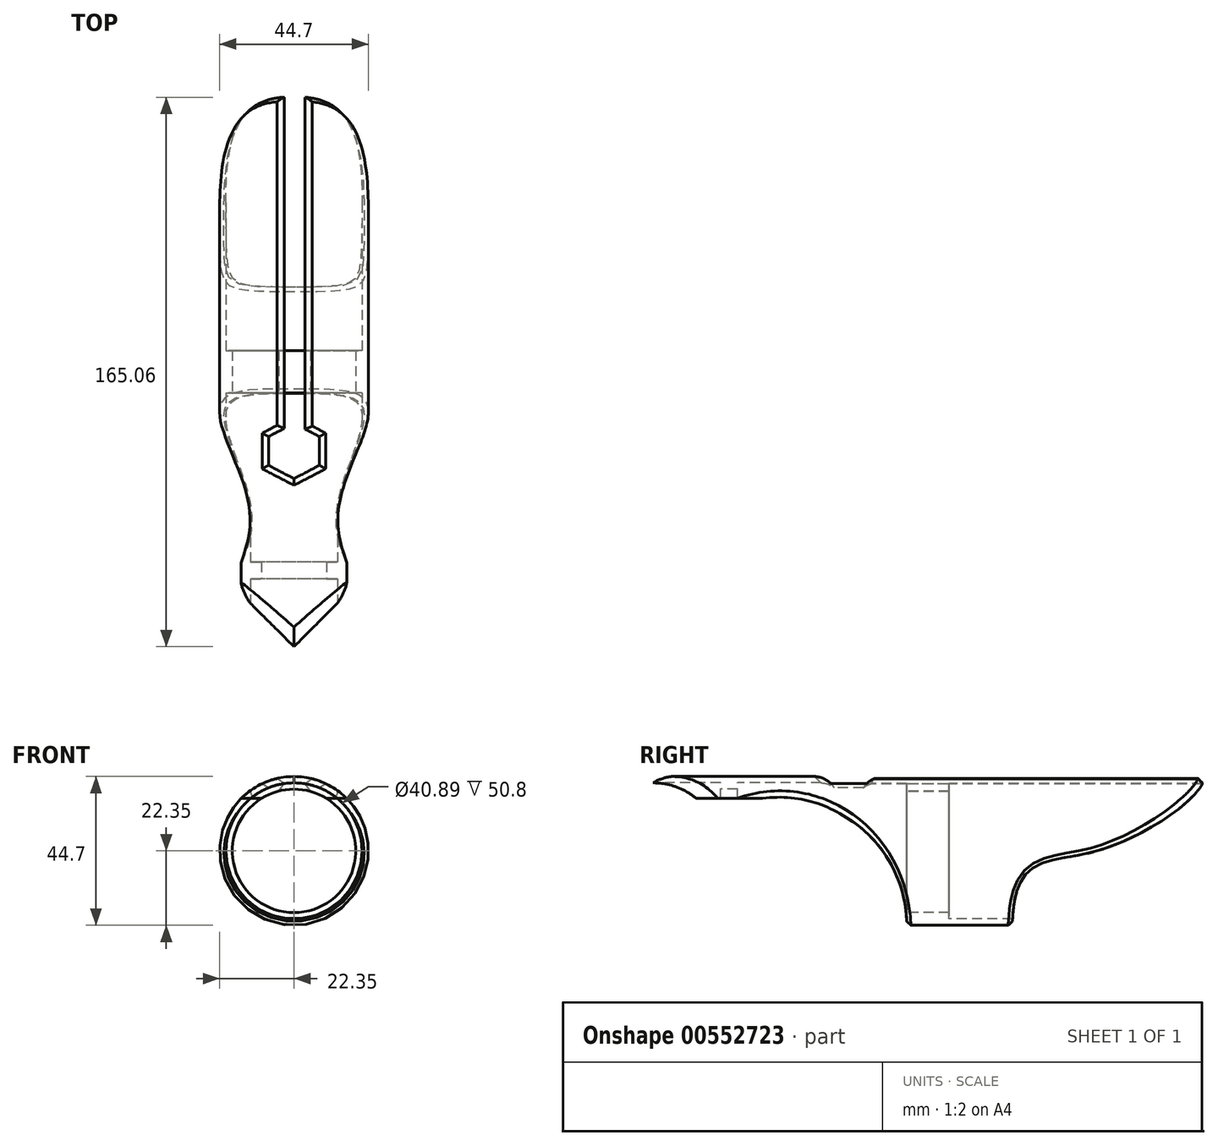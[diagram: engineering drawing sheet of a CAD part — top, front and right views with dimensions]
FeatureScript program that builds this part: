
annotation { "Feature Type Name" : "Feature", "Feature Type Description" : "" }
export const myFeature = defineFeature(function(context is Context, id is Id, definition is map)
    precondition{}
    {
        {
            var Q0;
            Q0=qCreatedBy(makeId("Front.planeOp"),FACE);
            var sketch = newSketch(context, id + "F0", { "sketchPlane" : qUnion([Q0])});
            skCircle(sketch, "E0", {"center": v(0, 0) * mm, "radius": 22.35 * mm});
            skCircle(sketch, "E1", {"center": v(0, 0) * mm, "radius": 20.45 * mm});
            skSolve(sketch);
        }
        {
            var Q0;
            Q0=qSketchRegion(id+"F0",true);
            extrude(context, id + "F1", {"entities" : qUnion([Q0]), "oppositeDirection" : true, "depth" : 165.1 * mm, "offsetDistance" : 25.4 * mm});
        }
        {
            var Q0;
            Q0=qCreatedBy(makeId("Front.planeOp"),FACE);
            var sketch = newSketch(context, id + "F2", { "sketchPlane" : qUnion([Q0])});
            skCircle(sketch, "E2", {"center": v(0, 0) * mm, "radius": 18.54 * mm});
            skCircle(sketch, "E3", {"center": v(0, 0) * mm, "radius": 21.84 * mm});
            skSolve(sketch);
        }
        {
            var Q0;
            Q0 = qSketchRegion(id + "F2", true);
            extrude(context, id + "F3", {"entities" : qUnion([Q0]), "operationType" : NewBodyOperationType.ADD, "oppositeDirection" : true, "depth" : 88.9 * mm, "offsetDistance" : 25.4 * mm, "hasSecondDirection" : true, "secondDirectionOppositeDirection" : true, "secondDirectionDepth" : 76.2 * mm});
        }
        {
            var Q0;
            Q0 = qSketchRegion(id + "F2", true);
            extrude(context, id + "F4", {"entities" : qUnion([Q0]), "operationType" : NewBodyOperationType.ADD, "oppositeDirection" : true, "depth" : 25.4 * mm, "offsetDistance" : 25.4 * mm, "hasSecondDirection" : true, "secondDirectionOppositeDirection" : true, "secondDirectionDepth" : 20.32 * mm});
        }
        {
            var Q0;
            Q0=qCreatedBy(makeId("Right.planeOp"),FACE);
            var sketch = newSketch(context, id + "F5", { "sketchPlane" : qUnion([Q0])});
            skLineSegment(sketch, "E4", {"start": v(0, -22.35) * mm, "end": v(76.2, -22.35) * mm});
            skLineSegment(sketch, "E5", {"start": v(107.95, -22.35) * mm, "end": v(165.1, -22.35) * mm});
            skLineSegment(sketch, "E6", {"start": v(165.1, 22.35) * mm, "end": v(165.1, -22.35) * mm});
            skLineSegment(sketch, "E7", {"start": v(0, 15.75) * mm, "end": v(0, -22.35) * mm});
            skLineSegment(sketch, "E8", {"start": v(0, 15.75) * mm, "end": v(38.1, 15.75) * mm});
            skArc(sketch, "E9", {"start": v(76.2, -22.35) * mm, "mid": v(65.04, 4.59) * mm, "end": v(38.1, 15.75) * mm});
            skLineSegment(sketch, "E10", {"start": v(165.1, 22.35) * mm, "end": v(165.1, 19.84) * mm});
            skFitSpline(sketch, "E11", {"points": [v(165.1, 22.35) * mm, v(133.35, 0) * mm, v(107.95, -22.35) * mm], "startDerivative": vector(12.5, -27.5) * mm, "endDerivative": vector(-2.14, -138.9) * mm});
            skSolve(sketch);
        }
        {
            var Q0;
            Q0=qSketchRegion(id+"F5",true);
            extrude(context, id + "F6", {"entities" : qUnion([Q0]), "operationType" : NewBodyOperationType.REMOVE, "endBound" : BoundingType.SYMMETRIC, "oppositeDirection" : true, "depth" : 50.8 * mm, "offsetDistance" : 25.4 * mm});
        }
        {
            var Q0;
            Q0=qCreatedBy(makeId("Top.planeOp"),FACE);
            var sketch = newSketch(context, id + "F7", { "sketchPlane" : qUnion([Q0])});
            skCircle(sketch, "E12.cCircle", {"center": v(0, 58.8) * mm, "radius": 8 * mm, "construction": true});
            skLineSegment(sketch, "E12.0", {"start": v(0, 50.8) * mm, "end": v(-6.93, 54.8) * mm});
            skLineSegment(sketch, "E12.1", {"start": v(-6.93, 54.8) * mm, "end": v(-6.93, 62.8) * mm});
            skLineSegment(sketch, "E12.2", {"start": v(-6.93, 62.8) * mm, "end": v(0, 66.8) * mm});
            skLineSegment(sketch, "E12.3", {"start": v(0, 66.8) * mm, "end": v(6.93, 62.8) * mm});
            skLineSegment(sketch, "E12.4", {"start": v(6.93, 62.8) * mm, "end": v(6.93, 54.8) * mm});
            skLineSegment(sketch, "E12.5", {"start": v(6.93, 54.8) * mm, "end": v(0, 50.8) * mm});
            skSolve(sketch);
        }
        {
            var Q0;
            Q0=qCreatedBy(makeId("Top.planeOp"),FACE);
            var sketch = newSketch(context, id + "F8", { "sketchPlane" : qUnion([Q0])});
            skPoint(sketch, "E13.0.midPoint", {"position": v(0, 0) * mm});
            skLineSegment(sketch, "E14", {"start": v(-28.56, 28.44) * mm, "end": v(0, 0) * mm});
            skLineSegment(sketch, "E15", {"start": v(0, 0) * mm, "end": v(28.33, 28.44) * mm});
            skArc(sketch, "E16", {"start": v(28.33, 28.44) * mm, "mid": v(0.08, -40.14) * mm, "end": v(-28.44, 28.33) * mm});
            skSolve(sketch);
        }
        {
            var Q0;
            Q0=qCreatedBy(makeId("Top.planeOp"),FACE);
            var sketch = newSketch(context, id + "F9", { "sketchPlane" : qUnion([Q0])});
            skLineSegment(sketch, "E17.bottom", {"start": v(-2.34, 60.13) * mm, "end": v(2.74, 60.13) * mm});
            skLineSegment(sketch, "E17.top", {"start": v(-2.34, 166.2) * mm, "end": v(2.74, 166.2) * mm});
            skLineSegment(sketch, "E17.left", {"start": v(-2.34, 60.13) * mm, "end": v(-2.34, 166.2) * mm});
            skLineSegment(sketch, "E17.right", {"start": v(2.74, 60.13) * mm, "end": v(2.74, 166.2) * mm});
            skSolve(sketch);
        }
        {
            var Q0;
            Q0=qSketchRegion(id+"F8",true);
            var Q1;
            Q1 = qSketchRegion(id + "F7", true);
            var Q2;
            Q2 = qSketchRegion(id + "F9", true);
            extrude(context, id + "F10", {"entities" : qUnion([Q0, Q1, Q2]), "operationType" : NewBodyOperationType.REMOVE, "depth" : 25.4 * mm, "offsetDistance" : 25.4 * mm});
        }
        {
            var Q0;
            Q0=makeQuery(id+"F10.boolean.opBoolean","INTERSECT",EDGE,{"derivedFrom":[makeQuery(id+"F1.opExtrude","SWEPT_FACE",FACE,{"disambiguationData":[OSD([sQuery(id+"F0.wireOp",EDGE,"E0")])]}),makeQuery(id+"F10.opExtrude","SWEPT_FACE",FACE,{"disambiguationData":[OSD([sQuery(id+"F7.wireOp",EDGE,"E12.1")])]})]});
            var Q1;
            Q1=makeQuery(id+"F10.boolean.opBoolean","INTERSECT",EDGE,{"derivedFrom":[makeQuery(id+"F1.opExtrude","SWEPT_FACE",FACE,{"disambiguationData":[OSD([sQuery(id+"F0.wireOp",EDGE,"E0")])]}),makeQuery(id+"F10.opExtrude","SWEPT_FACE",FACE,{"disambiguationData":[OSD([sQuery(id+"F7.wireOp",EDGE,"E12.4")])]})]});
            chamfer(context, id + "F11", {"entities" : qUnion([Q0, Q1]), "chamferType" : ChamferType.TWO_OFFSETS, "width1" : 2.54 * mm, "oppositeDirection" : false, "width2" : 2.54 * mm, "tangentPropagation" : true});
        }
        {
            var Q0;
            Q0=makeQuery(id+"F10.boolean.opBoolean","INTERSECT",EDGE,{"derivedFrom":[makeQuery(id+"F1.opExtrude","SWEPT_FACE",FACE,{"disambiguationData":[OSD([sQuery(id+"F0.wireOp",EDGE,"E0")])]}),makeQuery(id+"F10.opExtrude","SWEPT_FACE",FACE,{"disambiguationData":[OSD([sQuery(id+"F7.wireOp",EDGE,"E12.0")])]})]});
            var Q1;
            Q1=makeQuery(id+"F10.boolean.opBoolean","INTERSECT",EDGE,{"derivedFrom":[makeQuery(id+"F1.opExtrude","SWEPT_FACE",FACE,{"disambiguationData":[OSD([sQuery(id+"F0.wireOp",EDGE,"E0")])]}),makeQuery(id+"F10.opExtrude","SWEPT_FACE",FACE,{"disambiguationData":[OSD([sQuery(id+"F7.wireOp",EDGE,"E12.5")])]})]});
            var Q2;
            Q2=makeQuery(id+"F10.boolean.opBoolean","INTERSECT",EDGE,{"derivedFrom":[makeQuery(id+"F1.opExtrude","SWEPT_FACE",FACE,{"disambiguationData":[OSD([sQuery(id+"F0.wireOp",EDGE,"E0")])]}),makeQuery(id+"F10.opExtrude","SWEPT_FACE",FACE,{"disambiguationData":[OSD([sQuery(id+"F7.wireOp",EDGE,"E12.3")])]})]});
            var Q3;
            Q3=makeQuery(id+"F10.boolean.opBoolean","INTERSECT",EDGE,{"derivedFrom":[makeQuery(id+"F1.opExtrude","SWEPT_FACE",FACE,{"disambiguationData":[OSD([sQuery(id+"F0.wireOp",EDGE,"E0")])]}),makeQuery(id+"F10.opExtrude","SWEPT_FACE",FACE,{"disambiguationData":[OSD([sQuery(id+"F7.wireOp",EDGE,"E12.2")])]})]});
            chamfer(context, id + "F12", {"entities" : qUnion([Q0, Q1, Q2, Q3]), "chamferType" : ChamferType.TWO_OFFSETS, "width1" : 2.67 * mm, "oppositeDirection" : false, "width2" : 2.54 * mm, "tangentPropagation" : true});
        }
        {
            var Q0;
            Q0=makeQuery(id+"F10.boolean.opBoolean","INTERSECT",EDGE,{"derivedFrom":[makeQuery(id+"F1.opExtrude","SWEPT_FACE",FACE,{"disambiguationData":[OSD([sQuery(id+"F0.wireOp",EDGE,"E0")])]}),makeQuery(id+"F10.opExtrude","SWEPT_FACE",FACE,{"disambiguationData":[OSD([sQuery(id+"F9.wireOp",EDGE,"E17.right")])]})]});
            var Q1;
            Q1=makeQuery(id+"F10.boolean.opBoolean","INTERSECT",EDGE,{"derivedFrom":[makeQuery(id+"F1.opExtrude","SWEPT_FACE",FACE,{"disambiguationData":[OSD([sQuery(id+"F0.wireOp",EDGE,"E0")])]}),makeQuery(id+"F10.opExtrude","SWEPT_FACE",FACE,{"disambiguationData":[OSD([sQuery(id+"F9.wireOp",EDGE,"E17.left")])]})]});
            chamfer(context, id + "F13", {"entities" : qUnion([Q0, Q1]), "chamferType" : ChamferType.TWO_OFFSETS, "width1" : 2.54 * mm, "oppositeDirection" : false, "width2" : 2.3 * mm, "tangentPropagation" : true});
        }
        {
            var Q0;
            Q0=makeQuery(id+"F6.boolean.opBoolean","INTERSECT",EDGE,{"derivedFrom":[makeQuery(id+"F1.opExtrude","SWEPT_FACE",FACE,{"disambiguationData":[OSD([sQuery(id+"F0.wireOp",EDGE,"E0")])]}),makeQuery(id+"F6.opExtrude","SWEPT_FACE",FACE,{"disambiguationData":[OSD([sQuery(id+"F5.wireOp",EDGE,"E11")])]})]});
            var Q1;
            Q1=makeQuery(id+"F6.boolean.opBoolean","INTERSECT",EDGE,{"derivedFrom":[makeQuery(id+"F1.opExtrude","SWEPT_FACE",FACE,{"disambiguationData":[OSD([sQuery(id+"F0.wireOp",EDGE,"E0")])]}),makeQuery(id+"F6.opExtrude","SWEPT_FACE",FACE,{"disambiguationData":[OSD([sQuery(id+"F5.wireOp",EDGE,"E9")])]})]});
            chamfer(context, id + "F14", {"entities" : qUnion([Q0, Q1]), "width" : 1.27 * mm});
        }
        {
            var Q0;
            Q0=makeQuery(id+"F10.boolean.opBoolean","INTERSECT",EDGE,{"derivedFrom":[makeQuery(id+"F1.opExtrude","SWEPT_FACE",FACE,{"disambiguationData":[OSD([sQuery(id+"F0.wireOp",EDGE,"E0")])]}),makeQuery(id+"F10.opExtrude","SWEPT_FACE",FACE,{"disambiguationData":[OSD([sQuery(id+"F8.wireOp",EDGE,"E14")])]})]});
            var Q1;
            Q1=makeQuery(id+"F10.boolean.opBoolean","INTERSECT",EDGE,{"derivedFrom":[makeQuery(id+"F1.opExtrude","SWEPT_FACE",FACE,{"disambiguationData":[OSD([sQuery(id+"F0.wireOp",EDGE,"E0")])]}),makeQuery(id+"F10.opExtrude","SWEPT_FACE",FACE,{"disambiguationData":[OSD([sQuery(id+"F8.wireOp",EDGE,"E15")])]})]});
            fillet(context, id + "F15", {"entities" : qUnion([Q0, Q1]), "radius" : 5.08 * mm, "tangentPropagation" : true, "rho" : 0.35, "crossSection" : FilletCrossSection.CONIC, "allowEdgeOverflow" : false});
        }
        {
            var Q0;
            Q0=makeQuery(id+"F10.boolean.opBoolean","INTERSECT",EDGE,{"derivedFrom":[makeQuery(id+"F3.opExtrude","SWEPT_FACE",FACE,{"disambiguationData":[OSD([sQuery(id+"F2.wireOp",EDGE,"E2")])]}),makeQuery(id+"F10.opExtrude","SWEPT_FACE",FACE,{"disambiguationData":[OSD([sQuery(id+"F9.wireOp",EDGE,"E17.right")])]})]});
            var Q1;
            Q1=makeQuery(id+"F10.boolean.opBoolean","INTERSECT",EDGE,{"derivedFrom":[makeQuery(id+"F3.opExtrude","SWEPT_FACE",FACE,{"disambiguationData":[OSD([sQuery(id+"F2.wireOp",EDGE,"E2")])]}),makeQuery(id+"F10.opExtrude","SWEPT_FACE",FACE,{"disambiguationData":[OSD([sQuery(id+"F9.wireOp",EDGE,"E17.left")])]})]});
            chamfer(context, id + "F16", {"entities" : qUnion([Q0, Q1]), "width" : 3.05 * mm, "tangentPropagation" : true});
        }
    });
